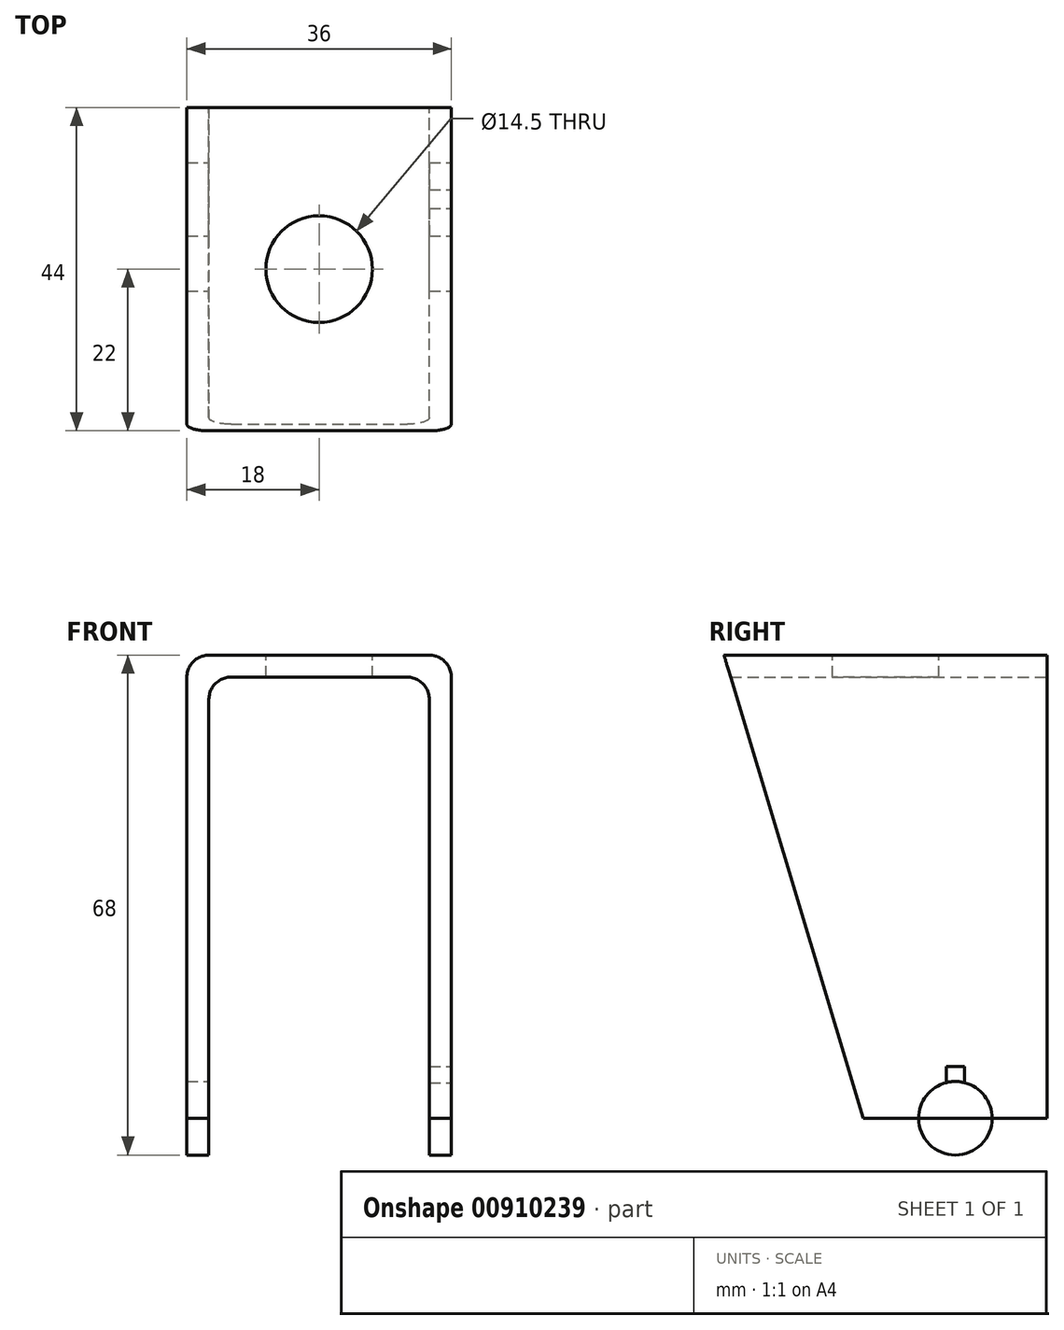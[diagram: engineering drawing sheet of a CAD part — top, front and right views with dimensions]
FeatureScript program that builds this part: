
annotation { "Feature Type Name" : "Feature", "Feature Type Description" : "" }
export const myFeature = defineFeature(function(context is Context, id is Id, definition is map)
    precondition{}
    {
        {
            var Q0;
            Q0=qCreatedBy(makeId("Front.planeOp"),FACE);
            var sketch = newSketch(context, id + "F0", { "sketchPlane" : qUnion([Q0])});
            skLineSegment(sketch, "E0", {"start": v(-33, 0) * mm, "end": v(-33, 70) * mm});
            skLineSegment(sketch, "E1", {"start": v(-33, 70) * mm, "end": v(-3, 70) * mm});
            skLineSegment(sketch, "E2", {"start": v(-3, 70) * mm, "end": v(-3, 0) * mm});
            skLineSegment(sketch, "E3", {"start": v(-36, 0) * mm, "end": v(-36, 73) * mm});
            skLineSegment(sketch, "E4", {"start": v(-36, 73) * mm, "end": v(0, 73) * mm});
            skLineSegment(sketch, "E5", {"start": v(0, 73) * mm, "end": v(0, 0) * mm});
            skLineSegment(sketch, "E6", {"start": v(0, 0) * mm, "end": v(-3, 0) * mm});
            skLineSegment(sketch, "E7", {"start": v(-33, 0) * mm, "end": v(-36, 0) * mm});
            skSolve(sketch);
        }
        {
            var Q0;
            Q0 = qSketchRegion(id + "F0", true);
            extrude(context, id + "F1", {"entities" : qUnion([Q0]), "depth" : 44 * mm, "offsetDistance" : 25 * mm});
        }
        {
            var Q0;
            Q0=makeQuery(id+"F1.opExtrude","SWEPT_FACE",FACE,{"disambiguationData":[OSD([sQuery(id+"F0.wireOp",EDGE,"E5")])]});
            var sketch = newSketch(context, id + "F2", { "sketchPlane" : qUnion([Q0])});
            skLineSegment(sketch, "E8", {"start": v(-44, 10) * mm, "end": v(0, 10) * mm});
            skLineSegment(sketch, "E9", {"start": v(-44, 73) * mm, "end": v(-22, 0) * mm});
            skSolve(sketch);
        }
        {
            var Q0;
            Q0 = qSketchRegion(id + "F2", true);
            var Q1;
            {var subQ0=sQuery(id+"F2.wireOp",EDGE,"E8");var subQ1=sQuery(id+"F0.wireOp",EDGE,"E5");var subQ2=makeQuery(id+"F1.opExtrude","CAP_EDGE",EDGE,{"disambiguationData":[OSD([subQ1])],"isStart":false});var subQ3=makeQuery(id+"F2.imprint","INTERSECT",VERTEX,{"derivedFrom":[subQ2,subQ0]});Q1=makeQuery(id+"F2.imprint","IMPRINT",FACE,{"disambiguationData":[TD([[makeQuery(id+"F2.imprint","IMPRINT",EDGE,{"disambiguationData":[TD([[subQ3,-1.0]])],"derivedFrom":subQ0}),1.0]])]});}
            var Q2;
            {var subQ0=sQuery(id+"F2.wireOp",EDGE,"E8");var subQ1=sQuery(id+"F0.wireOp",EDGE,"E5");var subQ2=makeQuery(id+"F1.opExtrude","CAP_EDGE",EDGE,{"disambiguationData":[OSD([subQ1])],"isStart":false});var subQ3=makeQuery(id+"F2.imprint","INTERSECT",VERTEX,{"derivedFrom":[subQ2,subQ0]});Q2=makeQuery(id+"F2.imprint","IMPRINT",FACE,{"disambiguationData":[TD([[makeQuery(id+"F2.imprint","IMPRINT",EDGE,{"disambiguationData":[TD([[subQ3,-1.0]])],"derivedFrom":subQ0}),-1.0]])]});}
            extrude(context, id + "F3", {"entities" : qUnion([Q0, Q1, Q2]), "operationType" : NewBodyOperationType.REMOVE, "oppositeDirection" : true, "depth" : 55.2 * mm, "offsetDistance" : 25 * mm});
        }
        {
            var Q0;
            Q0=makeQuery(id+"F1.opExtrude","SWEPT_FACE",FACE,{"disambiguationData":[OSD([sQuery(id+"F0.wireOp",EDGE,"E5")])]});
            var sketch = newSketch(context, id + "F4", { "sketchPlane" : qUnion([Q0])});
            skLineSegment(sketch, "E10", {"start": v(-25.01, 10) * mm, "end": v(0, 10) * mm});
            skCircle(sketch, "E11", {"center": v(-12.5, 10) * mm, "radius": 5 * mm});
            skArc(sketch, "E12", {"start": v(-25.01, 10) * mm, "mid": v(-12.5, -0.12) * mm, "end": v(0, 10) * mm});
            skSolve(sketch);
        }
        {
            var Q0;
            {var subQ0=sQuery(id+"F4.wireOp",EDGE,"E12");var subQ1=makeQuery(id+"F3.boolean.opBoolean","COPY",EDGE,{"derivedFrom":makeQuery(id+"F3.opExtrude","CAP_EDGE",EDGE,{"disambiguationData":[OSD([sQuery(id+"F2.wireOp",EDGE,"E9")])],"isStart":true})});var subQ3=makeQuery(id+"F4.imprint","INTERSECT",VERTEX,{"derivedFrom":[subQ1,subQ0]});Q0=makeQuery(id+"F4.imprint","IMPRINT",FACE,{"disambiguationData":[TD([[makeQuery(id+"F4.imprint","IMPRINT",EDGE,{"disambiguationData":[TD([[subQ3,1.0]])],"derivedFrom":subQ0}),1.0]])]});}
            var Q1;
            {var subQ0=sQuery(id+"F4.wireOp",EDGE,"E12");var subQ1=makeQuery(id+"F1.opExtrude","SWEPT_EDGE",EDGE,{"disambiguationData":[OSD([sQuery(id+"F0.wireOp",EDGE,"E5"),sQuery(id+"F0.wireOp",EDGE,"E6")])]});var subQ2=makeQuery(id+"F4.imprint","INTERSECT",VERTEX,{"disambiguationData":[OD(0.0)],"derivedFrom":[subQ1,subQ0]});Q1=makeQuery(id+"F4.imprint","IMPRINT",FACE,{"disambiguationData":[TD([[makeQuery(id+"F4.imprint","IMPRINT",EDGE,{"disambiguationData":[TD([[subQ2,-1.0]])],"derivedFrom":subQ0}),1.0]])]});}
            var Q2;
            {var subQ0=sQuery(id+"F4.wireOp",EDGE,"E12");var subQ1=makeQuery(id+"F3.boolean.opBoolean","COPY",EDGE,{"derivedFrom":makeQuery(id+"F3.opExtrude","CAP_EDGE",EDGE,{"disambiguationData":[OSD([sQuery(id+"F2.wireOp",EDGE,"E9")])],"isStart":true})});var subQ2=makeQuery(id+"F4.imprint","INTERSECT",VERTEX,{"derivedFrom":[subQ1,subQ0]});Q2=makeQuery(id+"F4.imprint","IMPRINT",FACE,{"disambiguationData":[TD([[makeQuery(id+"F4.imprint","IMPRINT",EDGE,{"disambiguationData":[TD([[subQ2,-1.0]])],"derivedFrom":subQ0}),-1.0]])]});}
            var Q3;
            {var subQ0=sQuery(id+"F4.wireOp",EDGE,"E12");var subQ1=sQuery(id+"F0.wireOp",EDGE,"E5");var subQ2=makeQuery(id+"F1.opExtrude","CAP_EDGE",EDGE,{"disambiguationData":[OSD([subQ1])],"isStart":true});var subQ3=makeQuery(id+"F4.imprint","INTERSECT",VERTEX,{"derivedFrom":[subQ2,sQuery(id+"F4.wireOp",EDGE,"E10"),subQ0]});Q3=makeQuery(id+"F4.imprint","IMPRINT",FACE,{"disambiguationData":[TD([[makeQuery(id+"F4.imprint","IMPRINT",EDGE,{"disambiguationData":[TD([[subQ3,1.0]])],"derivedFrom":subQ0}),-1.0]])]});}
            extrude(context, id + "F5", {"entities" : qUnion([Q0, Q1, Q2, Q3]), "operationType" : NewBodyOperationType.REMOVE, "oppositeDirection" : true, "depth" : 63.6 * mm, "offsetDistance" : 25 * mm});
        }
        {
            var Q0;
            {var subQ0=sQuery(id+"F4.wireOp",EDGE,"E11");var subQ1=sQuery(id+"F4.wireOp",EDGE,"E10");var subQ2=makeQuery(id+"F4.imprint","INTERSECT",VERTEX,{"disambiguationData":[OD(0.0)],"derivedFrom":[subQ1,subQ0]});Q0=makeQuery(id+"F4.imprint","IMPRINT",FACE,{"disambiguationData":[TD([[makeQuery(id+"F4.imprint","IMPRINT",EDGE,{"disambiguationData":[TD([[subQ2,-1.0]])],"derivedFrom":subQ1}),-1.0]])]});}
            var sketch = newSketch(context, id + "F6", { "sketchPlane" : qUnion([Q0])});
            skSolve(sketch);
        }
        {
            var Q0;
            {var subQ0=sQuery(id+"F4.wireOp",EDGE,"E11");var subQ1=sQuery(id+"F4.wireOp",EDGE,"E10");var subQ2=makeQuery(id+"F4.imprint","INTERSECT",VERTEX,{"disambiguationData":[OD(0.0)],"derivedFrom":[subQ1,subQ0]});Q0=makeQuery(id+"F4.imprint","IMPRINT",FACE,{"disambiguationData":[TD([[makeQuery(id+"F4.imprint","IMPRINT",EDGE,{"disambiguationData":[TD([[subQ2,-1.0]])],"derivedFrom":subQ1}),1.0]])]});}
            var Q1;
            {var subQ0=sQuery(id+"F4.wireOp",EDGE,"E11");var subQ1=sQuery(id+"F4.wireOp",EDGE,"E10");var subQ2=makeQuery(id+"F4.imprint","INTERSECT",VERTEX,{"disambiguationData":[OD(0.0)],"derivedFrom":[subQ1,subQ0]});Q1=makeQuery(id+"F6.imprint","IMPRINT",FACE,{"disambiguationData":[TD([[makeQuery(id+"F6.imprint","IMPRINT",EDGE,{"derivedFrom":makeQuery(id+"F4.imprint","IMPRINT",EDGE,{"disambiguationData":[TD([[subQ2,-1.0]])],"derivedFrom":subQ1})}),-1.0]])]});}
            extrude(context, id + "F7", {"entities" : qUnion([Q0, Q1]), "operationType" : NewBodyOperationType.REMOVE, "oppositeDirection" : true, "depth" : 49.8 * mm, "offsetDistance" : 25 * mm});
        }
        {
            var Q0;
            {var subQ0=sQuery(id+"F0.wireOp",EDGE,"E5");var subQ1=makeQuery(id+"F1.opExtrude","SWEPT_EDGE",EDGE,{"disambiguationData":[OSD([sQuery(id+"F0.wireOp",EDGE,"E4"),subQ0])]});Q0=makeQuery(id+"F4.imprint","IMPRINT",FACE,{"disambiguationData":[TD([[makeQuery(id+"F4.imprint","IMPRINT",EDGE,{"derivedFrom":subQ1}),-1.0]])]});}
            var sketch = newSketch(context, id + "F8", { "sketchPlane" : qUnion([Q0])});
            skLineSegment(sketch, "E13.bottom", {"start": v(-13.74, 17.01) * mm, "end": v(-11.24, 17.01) * mm});
            skLineSegment(sketch, "E13.top", {"start": v(-13.74, 13.01) * mm, "end": v(-11.24, 13.01) * mm});
            skLineSegment(sketch, "E13.left", {"start": v(-13.74, 17.01) * mm, "end": v(-13.74, 13.01) * mm});
            skLineSegment(sketch, "E13.right", {"start": v(-11.24, 17.01) * mm, "end": v(-11.24, 13.01) * mm});
            skPoint(sketch, "E13.middle", {"position": v(-12.49, 15.01) * mm});
            skSolve(sketch);
        }
        {
            var Q0;
            {var subQ0=sQuery(id+"F8.wireOp",EDGE,"E13.bottom");Q0=makeQuery(id+"F8.imprint","IMPRINT",FACE,{"disambiguationData":[TD([[makeQuery(id+"F8.imprint","IMPRINT",EDGE,{"derivedFrom":subQ0}),-1.0]])]});}
            var Q1;
            {var subQ0=sQuery(id+"F8.wireOp",EDGE,"E13.top");Q1=makeQuery(id+"F8.imprint","IMPRINT",FACE,{"disambiguationData":[TD([[makeQuery(id+"F8.imprint","IMPRINT",EDGE,{"derivedFrom":subQ0}),1.0]])]});}
            extrude(context, id + "F9", {"entities" : qUnion([Q0, Q1]), "operationType" : NewBodyOperationType.REMOVE, "oppositeDirection" : true, "depth" : 25 * mm, "offsetDistance" : 25 * mm});
        }
        {
            var Q0;
            Q0=makeQuery(id+"F1.opExtrude","SWEPT_FACE",FACE,{"disambiguationData":[OSD([sQuery(id+"F0.wireOp",EDGE,"E4")])]});
            var sketch = newSketch(context, id + "F10", { "sketchPlane" : qUnion([Q0])});
            skCircle(sketch, "E14", {"center": v(-18, -22) * mm, "radius": 7.25 * mm});
            skPoint(sketch, "E15.orphan", {"position": v(-36, -44) * mm});
            skPoint(sketch, "E16.end.orphan", {"position": v(0, 0) * mm});
            skSolve(sketch);
        }
        {
            var Q0;
            Q0 = qSketchRegion(id + "F10", true);
            extrude(context, id + "F11", {"entities" : qUnion([Q0]), "operationType" : NewBodyOperationType.REMOVE, "oppositeDirection" : true, "depth" : 25 * mm, "offsetDistance" : 25 * mm});
        }
        {
            var Q0;
            Q0=makeQuery(id+"F1.opExtrude","SWEPT_EDGE",EDGE,{"disambiguationData":[OSD([sQuery(id+"F0.wireOp",EDGE,"E4"),sQuery(id+"F0.wireOp",EDGE,"E5")])]});
            fillet(context, id + "F12", {"entities" : qUnion([Q0]), "radius" : 3 * mm, "tangentPropagation" : true, "allowEdgeOverflow" : false});
        }
        {
            var Q0;
            Q0=makeQuery(id+"F1.opExtrude","SWEPT_EDGE",EDGE,{"disambiguationData":[OSD([sQuery(id+"F0.wireOp",EDGE,"E3"),sQuery(id+"F0.wireOp",EDGE,"E4")])]});
            fillet(context, id + "F13", {"entities" : qUnion([Q0]), "radius" : 3 * mm, "tangentPropagation" : true, "allowEdgeOverflow" : false});
        }
        {
            var Q0;
            Q0=makeQuery(id+"F1.opExtrude","SWEPT_EDGE",EDGE,{"disambiguationData":[OSD([sQuery(id+"F0.wireOp",EDGE,"E0"),sQuery(id+"F0.wireOp",EDGE,"E1")])]});
            fillet(context, id + "F14", {"entities" : qUnion([Q0]), "radius" : 3 * mm, "tangentPropagation" : true, "allowEdgeOverflow" : false});
        }
        {
            var Q0;
            Q0=makeQuery(id+"F1.opExtrude","SWEPT_EDGE",EDGE,{"disambiguationData":[OSD([sQuery(id+"F0.wireOp",EDGE,"E1"),sQuery(id+"F0.wireOp",EDGE,"E2")])]});
            fillet(context, id + "F15", {"entities" : qUnion([Q0]), "radius" : 3 * mm, "tangentPropagation" : true, "allowEdgeOverflow" : false});
        }
    });
